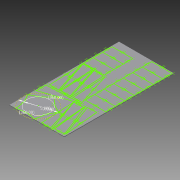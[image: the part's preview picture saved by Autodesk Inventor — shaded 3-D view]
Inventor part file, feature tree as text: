
AUTODESK INVENTOR PART (.ipt)
format: ipt  version: 2015 (Build 190159000, 159)  size: 222,208 bytes
history: native  units: in
note: dims shown in document units (in); Inventor stores cm internally (conversion verified against a paired STEP export)
features: sketch x2, extrude x1
ambient origin geometry x8: Origin, YZ Plane, XZ Plane, XY Plane, X Axis, Y Axis, Z Axis, Center Point
bodies: Solid1 (feature_tree)
feature tree (3):
  extrude  "Extrusion1"  Depth=24.0in
  sketch  "Sketch2"  dims[d2=0.125in d3=0.0in d5=1.9685in d7=1.9685in d8=5.0in d9=7.0in d10=360.0deg d11=360.0deg d13=1.9685in d15=1.9685in d17=1.9685in d19=1.9685in d21=1.9685in d23=1.9685in d25=1.9685in d27=1.9685in d29=1.9685in d31=1.9685in d33=1.9685in d35=1.9685in d37=1.9685in d39=1.9685in d41=1.9685in d43=1.9685in d45=1.9685in d47=1.9685in d49=1.9685in d51=1.9685in d53=1.9685in d55=1.9685in d57=1.9685in d59=1.9685in d61=1.9685in d63=1.9685in d65=1.9685in d67=1.9685in d69=1.9685in d71=1.9685in d73=1.9685in d75=1.9685in]
  sketch  "Sketch1"  dims[d0=12.0in d1=24.0in]
